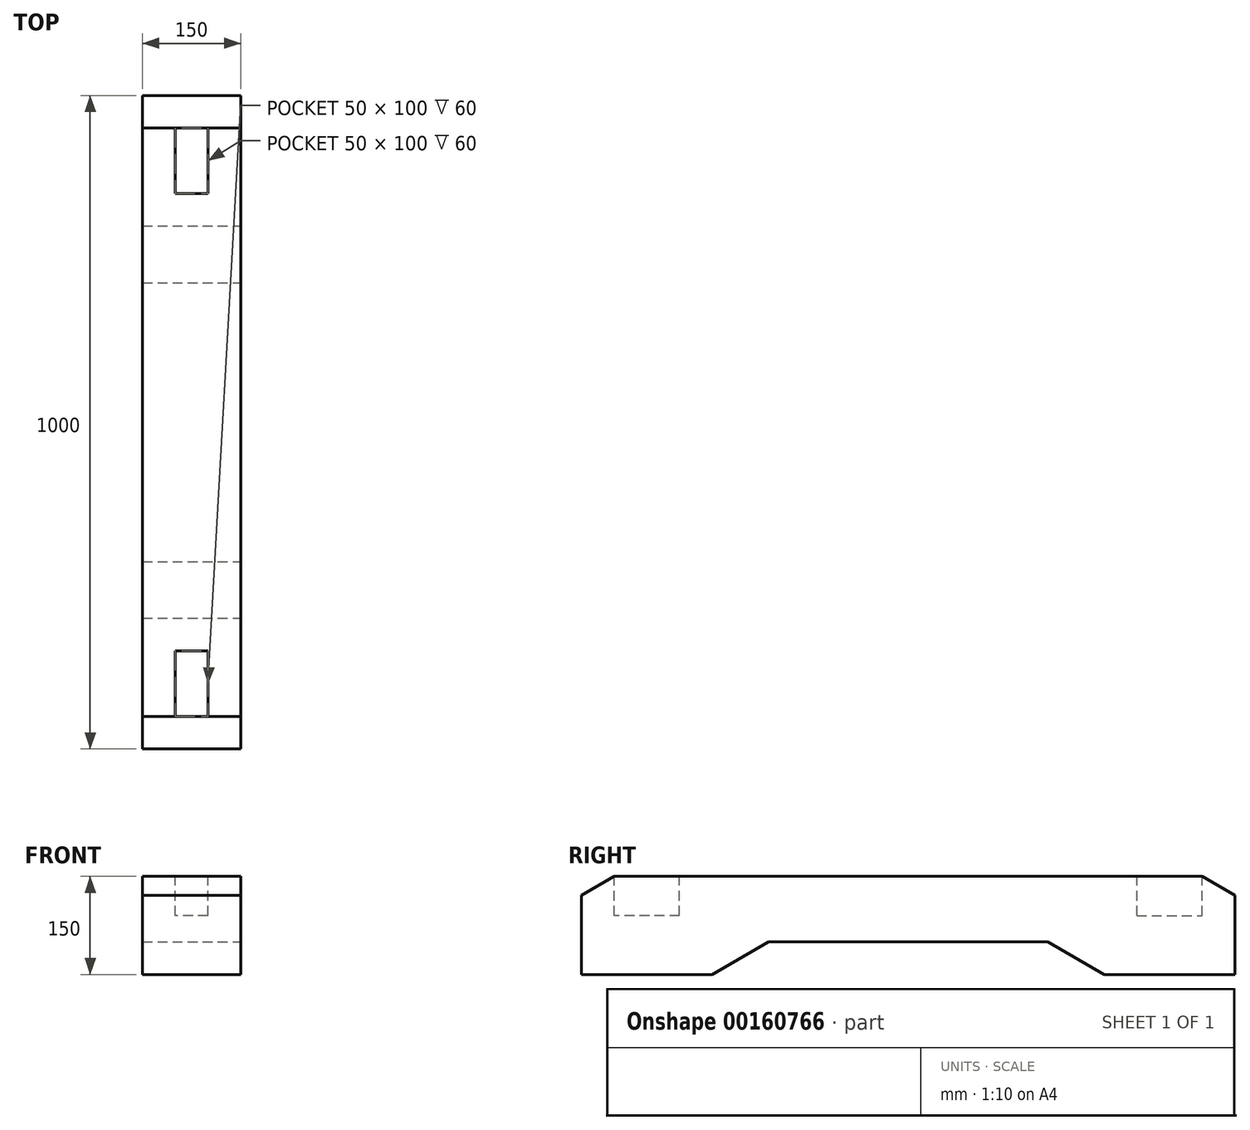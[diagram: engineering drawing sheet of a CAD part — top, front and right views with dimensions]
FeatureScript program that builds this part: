
annotation { "Feature Type Name" : "Feature", "Feature Type Description" : "" }
export const myFeature = defineFeature(function(context is Context, id is Id, definition is map)
    precondition{}
    {
        {
            assignVariable(context, id + "F0", {"name" : "B", "anyValue" : 150 * mm});
        }
        {
            assignVariable(context, id + "F1", {"name" : "L", "anyValue" : 1000 * mm});
        }
        {
            assignVariable(context, id + "F2", {"name" : "t_Tasche", "anyValue" : 60 * mm});
        }
        {
            var Q0;
            Q0=qCreatedBy(makeId("Front.planeOp"),FACE);
            var sketch = newSketch(context, id + "F3", { "sketchPlane" : qUnion([Q0])});
            skLineSegment(sketch, "E0.bottom", {"start": v(75, -75) * mm, "end": v(-75, -75) * mm});
            skLineSegment(sketch, "E0.top", {"start": v(75, 75) * mm, "end": v(-75, 75) * mm});
            skLineSegment(sketch, "E0.left", {"start": v(75, -75) * mm, "end": v(75, 75) * mm});
            skLineSegment(sketch, "E0.right", {"start": v(-75, -75) * mm, "end": v(-75, 75) * mm});
            skPoint(sketch, "E0.middle", {"position": v(0, 0) * mm});
            skSolve(sketch);
        }
        {
            var Q0;
            Q0 = qSketchRegion(id + "F3", true);
            extrude(context, id + "F4", {"entities" : qUnion([Q0]), "endBound" : BoundingType.SYMMETRIC, "depth" : getVariable(context, 'L')});
        }
        {
            var Q0;
            Q0=qCreatedBy(makeId("Right.planeOp"),FACE);
            var sketch = newSketch(context, id + "F5", { "sketchPlane" : qUnion([Q0])});
            skLineSegment(sketch, "E1", {"start": v(-500, 46.13) * mm, "end": v(-450, 75) * mm});
            skLineSegment(sketch, "E2", {"start": v(-300, -75) * mm, "end": v(-213.4, -25) * mm});
            skLineSegment(sketch, "E3", {"start": v(-213.4, -25) * mm, "end": v(0, -25) * mm});
            skLineSegment(sketch, "E4", {"start": v(0, -25) * mm, "end": v(0, -75) * mm, "construction": true});
            skLineSegment(sketch, "E5", {"start": v(0, -75) * mm, "end": v(-300, -75) * mm});
            skLineSegment(sketch, "E6", {"start": v(-450, 75) * mm, "end": v(-500, 75) * mm});
            skLineSegment(sketch, "E7", {"start": v(-500, 75) * mm, "end": v(-500, 46.13) * mm});
            skLineSegment(sketch, "E8.MirrorCS", {"start": v(213.4, -25) * mm, "end": v(0, -25) * mm});
            skLineSegment(sketch, "E9.MirrorCS", {"start": v(0, -75) * mm, "end": v(300, -75) * mm});
            skLineSegment(sketch, "E10.MirrorCS", {"start": v(300, -75) * mm, "end": v(213.4, -25) * mm});
            skLineSegment(sketch, "E11.MirrorCS", {"start": v(500, 46.13) * mm, "end": v(450, 75) * mm});
            skLineSegment(sketch, "E12.MirrorCS", {"start": v(450, 75) * mm, "end": v(500, 75) * mm});
            skLineSegment(sketch, "E13.MirrorCS", {"start": v(500, 75) * mm, "end": v(500, 46.13) * mm});
            skSolve(sketch);
        }
        {
            var Q0;
            Q0 = qSketchRegion(id + "F5", true);
            extrude(context, id + "F6", {"entities" : qUnion([Q0]), "operationType" : NewBodyOperationType.REMOVE, "endBound" : BoundingType.SYMMETRIC, "oppositeDirection" : true, "depth" : getVariable(context, 'B')});
        }
        {
            var Q0;
            Q0=makeQuery(id+"F4.opExtrude","SWEPT_FACE",FACE,{"disambiguationData":[OSD([sQuery(id+"F3.wireOp",EDGE,"E0.top")])]});
            var sketch = newSketch(context, id + "F7", { "sketchPlane" : qUnion([Q0])});
            skLineSegment(sketch, "E14.bottom", {"start": v(50, 350) * mm, "end": v(-50, 350) * mm, "construction": true});
            skLineSegment(sketch, "E14.top", {"start": v(50, 450) * mm, "end": v(-50, 450) * mm, "construction": true});
            skLineSegment(sketch, "E14.left", {"start": v(50, 350) * mm, "end": v(50, 450) * mm, "construction": true});
            skLineSegment(sketch, "E14.right", {"start": v(-50, 350) * mm, "end": v(-50, 450) * mm, "construction": true});
            skPoint(sketch, "E14.middle", {"position": v(0, 400) * mm});
            skLineSegment(sketch, "E15.bottom", {"start": v(50, -450) * mm, "end": v(-50, -450) * mm, "construction": true});
            skLineSegment(sketch, "E15.top", {"start": v(50, -350) * mm, "end": v(-50, -350) * mm, "construction": true});
            skLineSegment(sketch, "E15.left", {"start": v(50, -450) * mm, "end": v(50, -350) * mm, "construction": true});
            skLineSegment(sketch, "E15.right", {"start": v(-50, -450) * mm, "end": v(-50, -350) * mm, "construction": true});
            skPoint(sketch, "E15.middle", {"position": v(0, -400) * mm});
            skLineSegment(sketch, "E16", {"start": v(-75, 0) * mm, "end": v(75, 0) * mm, "construction": true});
            skLineSegment(sketch, "E17", {"start": v(0, 400) * mm, "end": v(0, 0) * mm, "construction": true});
            skLineSegment(sketch, "E18", {"start": v(0, 0) * mm, "end": v(0, -400) * mm, "construction": true});
            skLineSegment(sketch, "E19.bottom", {"start": v(25, 350) * mm, "end": v(-25, 350) * mm});
            skLineSegment(sketch, "E19.top", {"start": v(25, 450) * mm, "end": v(-25, 450) * mm});
            skLineSegment(sketch, "E19.left", {"start": v(25, 350) * mm, "end": v(25, 450) * mm});
            skLineSegment(sketch, "E19.right", {"start": v(-25, 350) * mm, "end": v(-25, 450) * mm});
            skLineSegment(sketch, "E20.MirrorCS", {"start": v(25, -350) * mm, "end": v(25, -450) * mm});
            skLineSegment(sketch, "E21.MirrorCS", {"start": v(25, -450) * mm, "end": v(-25, -450) * mm});
            skLineSegment(sketch, "E22.MirrorCS", {"start": v(-25, -350) * mm, "end": v(-25, -450) * mm});
            skLineSegment(sketch, "E23.MirrorCS", {"start": v(25, -350) * mm, "end": v(-25, -350) * mm});
            skSolve(sketch);
        }
        {
            var Q0;
            Q0 = qSketchRegion(id + "F7", true);
            extrude(context, id + "F8", {"entities" : qUnion([Q0]), "operationType" : NewBodyOperationType.REMOVE, "oppositeDirection" : true, "depth" : getVariable(context, 't_Tasche')});
        }
    });
